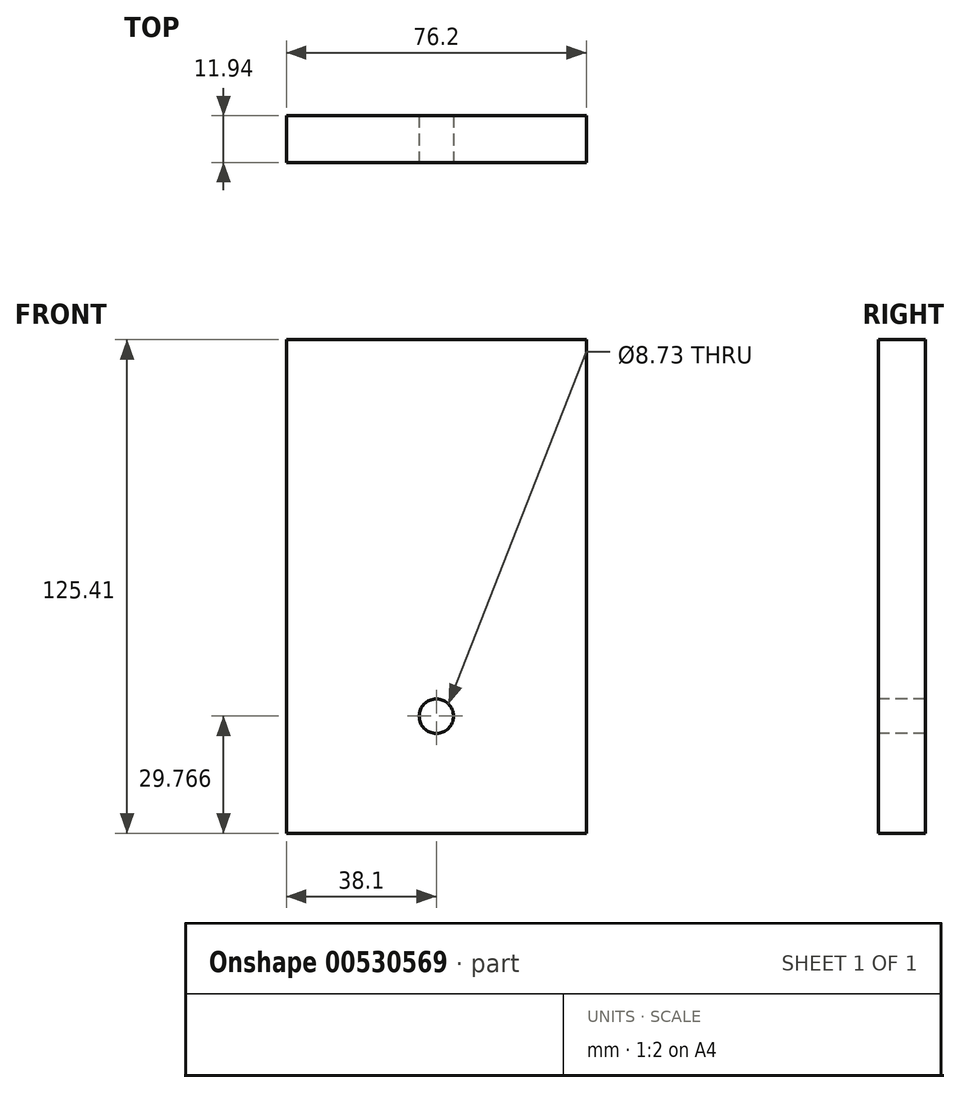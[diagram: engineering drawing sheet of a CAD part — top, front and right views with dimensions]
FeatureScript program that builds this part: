
annotation { "Feature Type Name" : "Feature", "Feature Type Description" : "" }
export const myFeature = defineFeature(function(context is Context, id is Id, definition is map)
    precondition{}
    {
        {
            var Q0;
            Q0=qCreatedBy(makeId("Front.planeOp"),FACE);
            var sketch = newSketch(context, id + "F0", { "sketchPlane" : qUnion([Q0])});
            skLineSegment(sketch, "E0.bottom", {"start": v(-76.2, 125.41) * mm, "end": v(0, 125.41) * mm});
            skLineSegment(sketch, "E0.top", {"start": v(-76.2, 0) * mm, "end": v(0, 0) * mm});
            skLineSegment(sketch, "E0.left", {"start": v(-76.2, 125.41) * mm, "end": v(-76.2, 0) * mm});
            skLineSegment(sketch, "E0.right", {"start": v(0, 125.41) * mm, "end": v(0, 0) * mm});
            skSolve(sketch);
        }
        {
            var Q0;
            Q0 = qSketchRegion(id + "F0", true);
            extrude(context, id + "F1", {"entities" : qUnion([Q0]), "depth" : 11.94 * mm, "offsetDistance" : 25.4 * mm});
        }
        {
            var Q0;
            Q0=makeQuery(id+"F1.opExtrude","CAP_FACE",FACE,{"disambiguationData":[OSD([sQuery(id+"F0.wireOp",EDGE,"E0.bottom"),sQuery(id+"F0.wireOp",EDGE,"E0.top"),sQuery(id+"F0.wireOp",EDGE,"E0.left"),sQuery(id+"F0.wireOp",EDGE,"E0.right")])],"isStart":false});
            var sketch = newSketch(context, id + "F2", { "sketchPlane" : qUnion([Q0])});
            skCircle(sketch, "E1", {"center": v(-38.1, 29.77) * mm, "radius": 4.37 * mm});
            skSolve(sketch);
        }
        {
            var Q0;
            Q0 = qSketchRegion(id + "F2", true);
            extrude(context, id + "F3", {"entities" : qUnion([Q0]), "operationType" : NewBodyOperationType.REMOVE, "endBound" : BoundingType.THROUGH_ALL, "oppositeDirection" : true, "depth" : 25.4 * mm, "offsetDistance" : 25.4 * mm});
        }
    });
